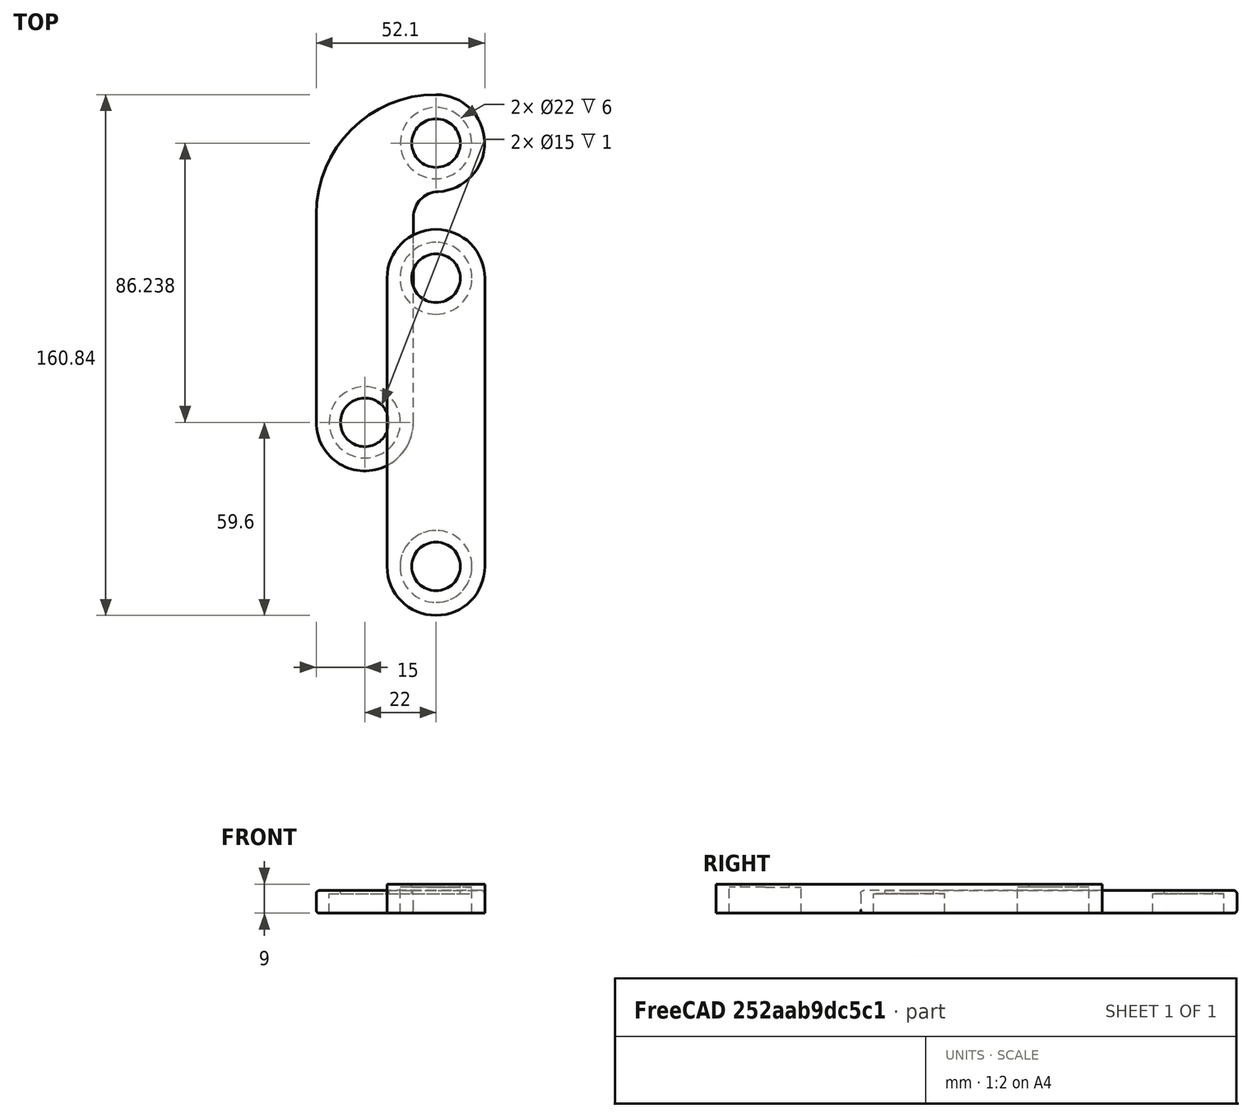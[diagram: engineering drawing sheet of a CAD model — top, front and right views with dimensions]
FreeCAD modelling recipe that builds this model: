
FCSTD DOCUMENT  (FreeCAD 0.20R29177 (Git))
Label: Фасовочник тяга
License: All rights reserved
LicenseURL: http://en.wikipedia.org/wiki/All_rights_reserved
objects: Sketcher::SketchObject×6, PartDesign::Body×3, PartDesign::Pad×2, PartDesign::Hole×2, PartDesign::Mirrored×2, Mesh::Feature×1, PartDesign::Fillet×1, PartDesign::MultiTransform×1
note: 22 computed .brp shape members not serialized (recipe doc carries the construction recipe); baked Part::Feature solids carry a one-line shape summary decoded from their .brp

FEATURE [Mesh::Feature] __________________________________________________2  label="поворот сортировщика семян2"
FEATURE [Sketcher::SketchObject] Sketch
  FullyConstrained = false
  MapMode = 5
  Support = -> [XY_Plane]
  sketch-geometry (12):
    g0: ArcOfCircle CenterX=0 CenterY=0 CenterZ=0 NormalX=0 NormalY=0 NormalZ=1 AngleXU=0 Radius=7.75 StartAngle=4.71239 EndAngle=7.85398
    g1: ArcOfCircle CenterX=0 CenterY=24 CenterZ=0 NormalX=0 NormalY=0 NormalZ=1 AngleXU=0 Radius=4.25 StartAngle=4.71239 EndAngle=7.85398
    g2: Circle CenterX=15.5 CenterY=0 CenterZ=0 NormalX=0 NormalY=0 NormalZ=1 AngleXU=0 Radius=4.25
    g3: ArcOfCircle CenterX=0 CenterY=24 CenterZ=0 NormalX=0 NormalY=0 NormalZ=1 AngleXU=0 Radius=10.9871 StartAngle=0.555851 EndAngle=1.5708
    g4: ArcOfCircle CenterX=15.5 CenterY=0 CenterZ=0 NormalX=0 NormalY=0 NormalZ=1 AngleXU=0 Radius=10.4846 StartAngle=5.70525 EndAngle=6.83904
    g5: LineSegment StartX=9.33299 StartY=29.7975 StartZ=0 EndX=24.4061 EndY=5.53236 EndZ=0
    g6: LineSegment StartX=1.3e-15 StartY=34.9871 StartZ=0 EndX=1.3e-15 EndY=28.25 EndZ=0
    g7: LineSegment StartX=2.4e-15 StartY=7.75 StartZ=0 EndX=2.4e-15 EndY=19.75 EndZ=0
    g8: LineSegment StartX=-1.4e-15 StartY=-7.75 StartZ=0 EndX=-1.4e-15 EndY=-24.9647 EndZ=0
    g9: LineSegment StartX=-1.4e-15 StartY=-24.9647 StartZ=0 EndX=5.98111 EndY=-24.9647 EndZ=0
    g10: LineSegment StartX=13.5023 StartY=-22.2553 StartZ=0 EndX=24.2818 EndY=-5.72764 EndZ=0
    g11: ArcOfCircle CenterX=7.94886 CenterY=-18.6332 CenterZ=0 NormalX=0 NormalY=0 NormalZ=1 AngleXU=0 Radius=6.63019 StartAngle=4.41106 EndAngle=5.70525
  constraints (29):
    c: Coincident(g0,g-1)
    c: Diameter(g0) = 15.5
    c: PointOnObject(g1,g-2)
    c: DistanceY(g1) = 24
    c: Diameter(g1) = 8.5
    c: PointOnObject(g2,g-1)
    c: Equal(g2,g1)
    c: DistanceX(g2) = 15.5
    c: Coincident(g3,g1)
    c: PointOnObject(g3,g-2)
    c: Coincident(g4,g2)
    c: Coincident(g6,g3)
    c: Vertical(g6)
    c: Vertical(g7)
    c: PointOnObject(g8,g-2)
    c: Vertical(g8)
    c: Coincident(g9,g8)
    c: Horizontal(g9)
    c: Coincident(g11,g9)
    c: Coincident(g0,g7)
    c: Coincident(g0,g8)
    c: Coincident(g1,g6)
    c: Coincident(g1,g7)
    c: Tangent(g10,g4) = -1.5708
    c: Tangent(g5,g4) = 1.5708
    c: Tangent(g5,g3) = 1.5708
    c: Tangent(g11,g10) = -1.5708
    c: PointOnObject(g0,g-2)
    c: DistanceY(g0,g1) = 16.25
FEATURE [Sketcher::SketchObject] Sketch001
  FullyConstrained = false
  MapMode = 5
  Placement = pos=(0,0,0) rot=(0.57735,0.57735,0.57735;2.0944rad)
  Support = -> [YZ_Plane]
  sketch-geometry (1):
    g0: LineSegment StartX=35.1772 StartY=-6.47577 StartZ=0 EndX=35.1772 EndY=6.52147 EndZ=0
  constraints (1):
    c: Vertical(g0)
FEATURE [PartDesign::Body] Body
  Group = -> [Sketch,Sketch001]
  Origin = -> Origin
FEATURE [Sketcher::SketchObject] Sketch002
  FullyConstrained = true
  MapMode = 5
  Support = -> [XY_Plane001]
  sketch-geometry (8):
    g0: Circle CenterX=4.6e-15 CenterY=86.238 CenterZ=0 NormalX=0 NormalY=0 NormalZ=1 AngleXU=0 Radius=11
    g1: ArcOfCircle CenterX=4.6e-15 CenterY=86.238 CenterZ=0 NormalX=0 NormalY=0 NormalZ=1 AngleXU=0 Radius=15 StartAngle=4.75588 EndAngle=7.85398
    g2: LineSegment StartX=-37 StartY=64.238 StartZ=0 EndX=-37 EndY=0 EndZ=0
    g3: LineSegment StartX=-7 StartY=0 StartZ=0 EndX=-7 EndY=63.2598 EndZ=0
    g4: ArcOfCircle CenterX=0 CenterY=64.238 CenterZ=0 NormalX=0 NormalY=0 NormalZ=1 AngleXU=0 Radius=37 StartAngle=1.5708 EndAngle=3.14159
    g5: ArcOfCircle CenterX=1 CenterY=63.2598 CenterZ=0 NormalX=0 NormalY=0 NormalZ=1 AngleXU=0 Radius=8 StartAngle=1.61429 EndAngle=3.14159
    g6: ArcOfCircle CenterX=-22 CenterY=0 CenterZ=0 NormalX=0 NormalY=0 NormalZ=1 AngleXU=0 Radius=15 StartAngle=3.14159 EndAngle=6.28319
    g7: Circle CenterX=-22 CenterY=0 CenterZ=0 NormalX=0 NormalY=0 NormalZ=1 AngleXU=0 Radius=11
  constraints (20):
    c: Coincident(g1,g0)
    c: Vertical(g2)
    c: Vertical(g3)
    c: Tangent(g2,g4) = -1.5708
    c: Diameter(g0) = 22
    c: Diameter(g1) = 30
    c: Tangent(g5,g3) = 1.5708
    c: Diameter(g5) = 16
    c: DistanceX(g3,g1) = 7
    c: Tangent(g5,g1) = 1.5708
    c: Tangent(g4,g1) = -1.5708
    c: Vertical(g1,g1)
    c: PointOnObject(g1,g-2)
    c: PointOnObject(g6,g-1)
    c: Coincident(g7,g6)
    c: Equal(g0,g7)
    c: Equal(g1,g6)
    c: Tangent(g6,g2) = -1.5708
    c: Tangent(g6,g3) = -1.5708
    c: Distance(g6,g1) = 89
FEATURE [PartDesign::Pad] Pad
  Direction = (0,0,1)
  Length = 7
  Length2 = 10
  Profile = -> Sketch002
  ReferenceAxis = -> Sketch002 [N_Axis]
  Type = 0
FEATURE [Sketcher::SketchObject] Sketch003
  FullyConstrained = true
  MapMode = 5
  Support = -> [XY_Plane001]
  expr: Constraints[19] = Sketch002.Constraints[19]
  expr: Constraints[4] = Sketch002.Constraints[4]
  expr: Constraints[5] = Sketch002.Constraints[5]
  expr: Constraints[7] = Sketch002.Constraints[7]
  expr: Constraints[8] = Sketch002.Constraints[8]
  sketch-geometry (8):
    g0: Circle CenterX=2.3e-15 CenterY=86.238 CenterZ=0 NormalX=0 NormalY=0 NormalZ=1 AngleXU=0 Radius=11
    g1: ArcOfCircle CenterX=2.3e-15 CenterY=86.238 CenterZ=0 NormalX=0 NormalY=0 NormalZ=1 AngleXU=0 Radius=15 StartAngle=4.75588 EndAngle=7.85398
    g2: LineSegment StartX=-37 StartY=64.238 StartZ=0 EndX=-37 EndY=0 EndZ=0
    g3: LineSegment StartX=-7 StartY=-3.7e-15 StartZ=0 EndX=-7 EndY=63.2598 EndZ=0
    g4: ArcOfCircle CenterX=0 CenterY=64.238 CenterZ=0 NormalX=0 NormalY=0 NormalZ=1 AngleXU=0 Radius=37 StartAngle=1.5708 EndAngle=3.14159
    g5: ArcOfCircle CenterX=1 CenterY=63.2598 CenterZ=0 NormalX=0 NormalY=0 NormalZ=1 AngleXU=0 Radius=8 StartAngle=1.61429 EndAngle=3.14159
    g6: ArcOfCircle CenterX=-22 CenterY=0 CenterZ=0 NormalX=0 NormalY=0 NormalZ=1 AngleXU=0 Radius=15 StartAngle=3.14159 EndAngle=6.28319
    g7: Circle CenterX=-22 CenterY=0 CenterZ=0 NormalX=0 NormalY=0 NormalZ=1 AngleXU=0 Radius=11
  constraints (20):
    c: Coincident(g1,g0)
    c: Vertical(g2)
    c: Vertical(g3)
    c: Tangent(g2,g4) = -1.5708
    c: Diameter(g0) = 22
    c: Diameter(g1) = 30
    c: Tangent(g5,g3) = 1.5708
    c: Diameter(g5) = 16
    c: DistanceX(g3,g1) = 7
    c: Tangent(g5,g1) = 1.5708
    c: Tangent(g4,g1) = -1.5708
    c: Vertical(g1,g1)
    c: PointOnObject(g1,g-2)
    c: PointOnObject(g6,g-1)
    c: Coincident(g7,g6)
    c: Equal(g0,g7)
    c: Equal(g1,g6)
    c: Tangent(g6,g2) = -1.5708
    c: Tangent(g6,g3) = -1.5708
    c: Distance(g6,g1) = 89
FEATURE [PartDesign::Hole] Hole
  BaseFeature = -> Pad
  CustomThreadClearance = 0
  Depth = 257.614
  DepthType = 1
  Diameter = 15
  DrillForDepth = false
  DrillPoint = 1
  DrillPointAngle = 118
  HoleCutCountersinkAngle = 50
  HoleCutCustomValues = false
  HoleCutDepth = 6
  HoleCutDiameter = 22
  HoleCutType = 1
  ModelThread = false
  Profile = -> Sketch003
  Reversed = true
  Tapered = false
  TaperedAngle = 90
  ThreadClass = 0
  ThreadDepth = 257.614
  ThreadDepthType = 0
  ThreadDirection = 0
  ThreadFit = 0
  ThreadSize = 0
  ThreadType = 0
  Threaded = false
  UseCustomThreadClearance = false
  expr: HoleCutDepth = Pad.Length - 1mm
FEATURE [PartDesign::Fillet] Fillet
  Base = -> Hole [Edge12,Edge17]
  BaseFeature = -> Hole
  Radius = 1
  SupportTransform = false
  UseAllEdges = false
FEATURE [PartDesign::Body] Body001
  Group = -> [Sketch002,Pad,Sketch003,Hole,Fillet]
  Origin = -> Origin001
  Tip = -> Fillet
FEATURE [Sketcher::SketchObject] Sketch004
  FullyConstrained = true
  MapMode = 5
  Support = -> [XY_Plane002]
  sketch-geometry (7):
    g0: ArcOfCircle CenterX=0 CenterY=44.5 CenterZ=0 NormalX=0 NormalY=0 NormalZ=1 AngleXU=0 Radius=11.1 StartAngle=4.71239 EndAngle=7.85398
    g1: ArcOfCircle CenterX=0 CenterY=44.5 CenterZ=0 NormalX=0 NormalY=0 NormalZ=1 AngleXU=0 Radius=15.1 StartAngle=0 EndAngle=1.5708
    g2: LineSegment StartX=0 StartY=55.6 StartZ=0 EndX=0 EndY=59.6 EndZ=0
    g3: LineSegment StartX=-2e-15 StartY=33.4 StartZ=0 EndX=0 EndY=0 EndZ=0
    g4: LineSegment StartX=0 StartY=0 StartZ=0 EndX=15.1 EndY=0 EndZ=0
    g5: LineSegment StartX=15.1 StartY=44.5 StartZ=0 EndX=15.1 EndY=0 EndZ=0
    g6: LineSegment StartX=-2e-15 StartY=33.4 StartZ=0 EndX=0 EndY=55.6 EndZ=0
  constraints (19):
    c: PointOnObject(g0,g-2)
    c: PointOnObject(g0,g-2)
    c: PointOnObject(g0,g-2)
    c: Coincident(g1,g0)
    c: PointOnObject(g1,g-2)
    c: Coincident(g2,g0)
    c: Coincident(g2,g1)
    c: Coincident(g3,g0)
    c: Coincident(g3,g-1)
    c: Coincident(g4,g3)
    c: PointOnObject(g4,g-1)
    c: Coincident(g5,g4)
    c: Vertical(g5)
    c: Diameter(g0) = 22.2
    c: Coincident(g6,g3)
    c: Coincident(g6,g2)
    c: Tangent(g5,g1) = 1.5708
    c: Distance(g2) = 4
    c: DistanceY(g1) = 44.5
FEATURE [PartDesign::Pad] Pad001
  Direction = (0,0,1)
  Length = 9
  Length2 = 10
  Profile = -> Sketch004
  ReferenceAxis = -> Sketch004 [N_Axis]
  Type = 0
FEATURE [Sketcher::SketchObject] Sketch005
  FullyConstrained = true
  MapMode = 5
  Support = -> [XY_Plane002]
  expr: Constraints[13] = Sketch004.Constraints[13]
  expr: Constraints[17] = Sketch004.Constraints[17]
  expr: Constraints[18] = Sketch004.Constraints[18]
  sketch-geometry (8):
    g0: ArcOfCircle CenterX=0 CenterY=44.5 CenterZ=0 NormalX=0 NormalY=0 NormalZ=1 AngleXU=0 Radius=11.1 StartAngle=4.71239 EndAngle=7.85398
    g1: ArcOfCircle CenterX=0 CenterY=44.5 CenterZ=0 NormalX=0 NormalY=0 NormalZ=1 AngleXU=0 Radius=15.1 StartAngle=0 EndAngle=1.5708
    g2: LineSegment StartX=0 StartY=55.6 StartZ=0 EndX=9e-16 EndY=59.6 EndZ=0
    g3: LineSegment StartX=-2e-15 StartY=33.4 StartZ=0 EndX=0 EndY=0 EndZ=0
    g4: LineSegment StartX=0 StartY=0 StartZ=0 EndX=15.1 EndY=0 EndZ=0
    g5: LineSegment StartX=15.1 StartY=44.5 StartZ=0 EndX=15.1 EndY=0 EndZ=0
    g6: LineSegment StartX=-2e-15 StartY=33.4 StartZ=0 EndX=0 EndY=55.6 EndZ=0
    g7: Circle CenterX=0 CenterY=44.5 CenterZ=0 NormalX=0 NormalY=0 NormalZ=1 AngleXU=0 Radius=11.1
  constraints (21):
    c: PointOnObject(g0,g-2)
    c: PointOnObject(g0,g-2)
    c: PointOnObject(g0,g-2)
    c: Coincident(g1,g0)
    c: PointOnObject(g1,g-2)
    c: Coincident(g2,g0)
    c: Coincident(g2,g1)
    c: Coincident(g3,g0)
    c: Coincident(g3,g-1)
    c: Coincident(g4,g3)
    c: PointOnObject(g4,g-1)
    c: Coincident(g5,g4)
    c: Vertical(g5)
    c: Diameter(g0) = 22.2
    c: Coincident(g6,g3)
    c: Coincident(g6,g2)
    c: Tangent(g5,g1) = 1.5708
    c: Distance(g2) = 4
    c: DistanceY(g1) = 44.5
    c: Coincident(g7,g0)
    c: PointOnObject(g0,g7)
FEATURE [PartDesign::Hole] Hole001
  BaseFeature = -> Pad001
  CustomThreadClearance = 0
  Depth = 132.762
  DepthType = 1
  Diameter = 15
  DrillForDepth = false
  DrillPoint = 1
  DrillPointAngle = 118
  HoleCutCountersinkAngle = 90
  HoleCutCustomValues = false
  HoleCutDepth = 8
  HoleCutDiameter = 22.2
  HoleCutType = 1
  ModelThread = false
  Profile = -> Sketch005
  Reversed = true
  Tapered = false
  TaperedAngle = 90
  ThreadClass = 0
  ThreadDepth = 132.762
  ThreadDepthType = 0
  ThreadDirection = 0
  ThreadFit = 0
  ThreadSize = 0
  ThreadType = 0
  Threaded = false
  UseCustomThreadClearance = false
  expr: HoleCutDepth = Pad001.Length - 1mm
FEATURE [PartDesign::Mirrored] Mirrored
  MirrorPlane = -> Sketch004 [V_Axis]
FEATURE [PartDesign::Mirrored] Mirrored001
  MirrorPlane = -> Sketch004 [H_Axis]
FEATURE [PartDesign::MultiTransform] MultiTransform
  BaseFeature = -> Hole001
  Originals = -> [Pad001,Hole001]
  Transformations = -> [Mirrored,Mirrored001]
FEATURE [PartDesign::Body] Body002
  Group = -> [Sketch004,Pad001,Sketch005,Hole001,MultiTransform,Mirrored,Mirrored001]
  Origin = -> Origin002
  Tip = -> MultiTransform
